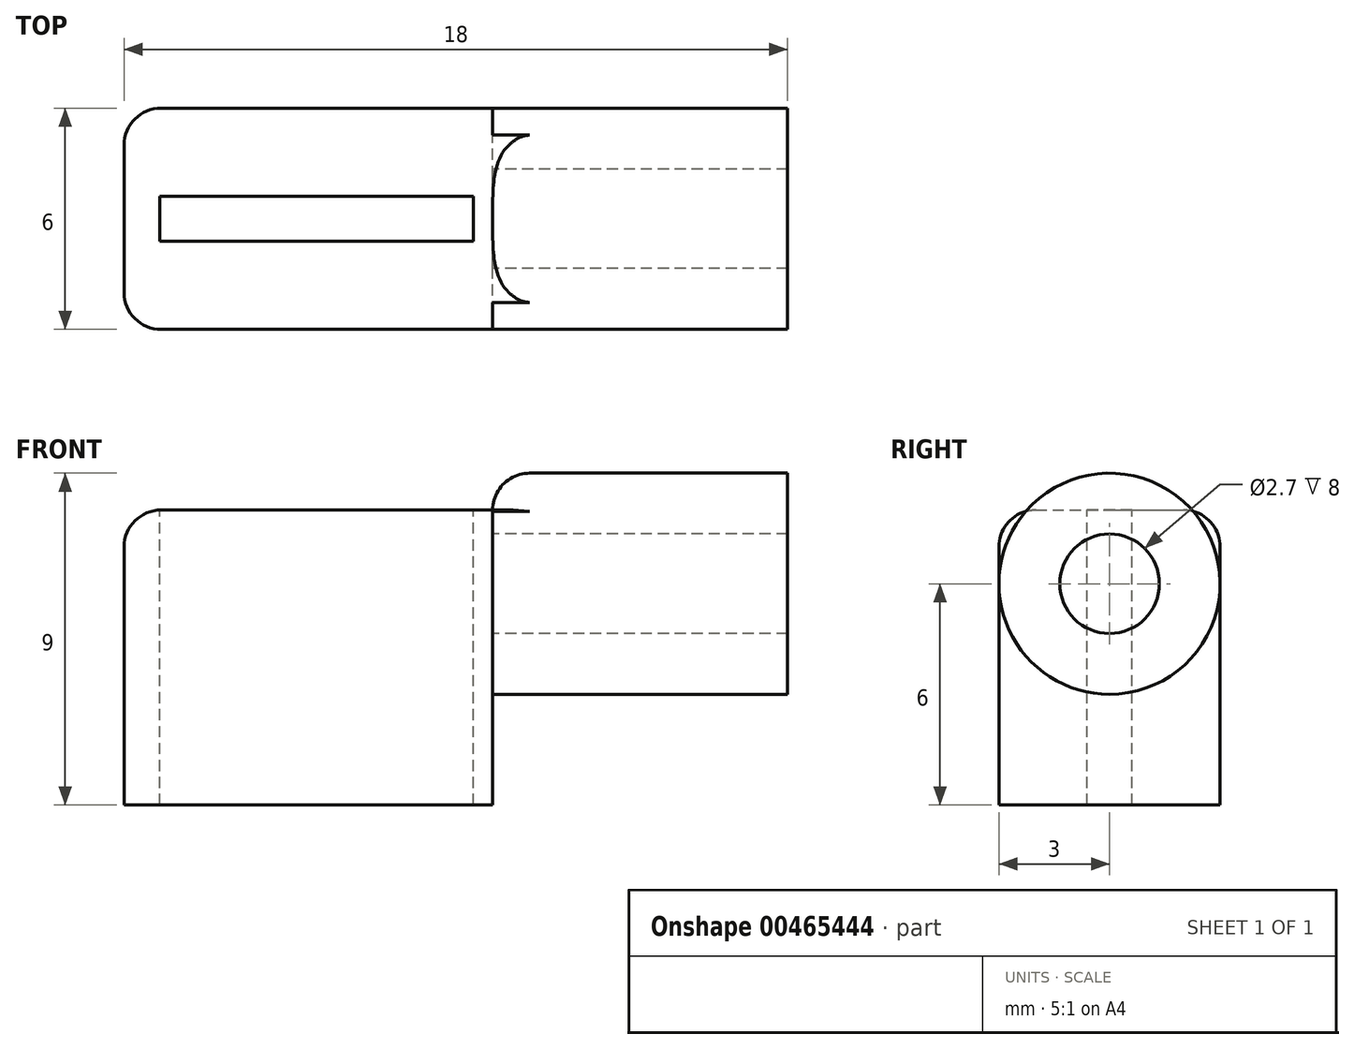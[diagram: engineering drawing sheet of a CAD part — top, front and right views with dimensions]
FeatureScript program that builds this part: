
annotation { "Feature Type Name" : "Feature", "Feature Type Description" : "" }
export const myFeature = defineFeature(function(context is Context, id is Id, definition is map)
    precondition{}
    {
        {
            var Q0;
            Q0=qCreatedBy(makeId("Right.planeOp"),FACE);
            var sketch = newSketch(context, id + "F0", { "sketchPlane" : qUnion([Q0])});
            skCircle(sketch, "E0", {"center": v(0, 0) * mm, "radius": 3 * mm});
            skCircle(sketch, "E1", {"center": v(0, 0) * mm, "radius": 1.35 * mm});
            skSolve(sketch);
        }
        {
            var Q0;
            Q0=makeQuery(id+"F0.imprint","IMPRINT",FACE,{"disambiguationData":[TD([[makeQuery(id+"F0.imprint","IMPRINT",EDGE,{"derivedFrom":sQuery(id+"F0.wireOp",EDGE,"E0")}),1.0]])]});
            extrude(context, id + "F1", {"entities" : qUnion([Q0]), "depth" : 8 * mm});
        }
        {
            var Q0;
            Q0=qCreatedBy(makeId("Top.planeOp"),FACE);
            var sketch = newSketch(context, id + "F2", { "sketchPlane" : qUnion([Q0])});
            skLineSegment(sketch, "E2.bottom", {"start": v(0, -3) * mm, "end": v(-10, -3) * mm});
            skLineSegment(sketch, "E2.top", {"start": v(0, 3) * mm, "end": v(-10, 3) * mm});
            skLineSegment(sketch, "E2.left", {"start": v(0, -3) * mm, "end": v(0, 3) * mm});
            skLineSegment(sketch, "E2.right", {"start": v(-10, -3) * mm, "end": v(-10, 3) * mm});
            skSolve(sketch);
        }
        {
            var Q0;
            Q0=makeQuery(id+"F2.imprint","IMPRINT",FACE,{"disambiguationData":[TD([[makeQuery(id+"F2.imprint","IMPRINT",EDGE,{"derivedFrom":sQuery(id+"F2.wireOp",EDGE,"E2.bottom")}),-1.0]])]});
            extrude(context, id + "F3", {"entities" : qUnion([Q0]), "operationType" : NewBodyOperationType.ADD, "depth" : 2 * mm});
        }
        {
            var Q0;
            Q0=makeQuery(id+"F3.opExtrude","CAP_FACE",FACE,{"disambiguationData":[OSD([sQuery(id+"F2.wireOp",EDGE,"E2.bottom"),sQuery(id+"F2.wireOp",EDGE,"E2.top"),sQuery(id+"F2.wireOp",EDGE,"E2.left"),sQuery(id+"F2.wireOp",EDGE,"E2.right")])],"isStart":true});
            extrude(context, id + "F4", {"entities" : qUnion([Q0]), "operationType" : NewBodyOperationType.ADD, "depth" : 6 * mm});
        }
        {
            var Q0;
            Q0=makeQuery(id+"F3.opExtrude","CAP_FACE",FACE,{"disambiguationData":[OSD([sQuery(id+"F2.wireOp",EDGE,"E2.bottom"),sQuery(id+"F2.wireOp",EDGE,"E2.top"),sQuery(id+"F2.wireOp",EDGE,"E2.left"),sQuery(id+"F2.wireOp",EDGE,"E2.right")])],"isStart":false});
            var sketch = newSketch(context, id + "F5", { "sketchPlane" : qUnion([Q0])});
            skLineSegment(sketch, "E3.bottom", {"start": v(-9.03, 0.61) * mm, "end": v(-0.53, 0.61) * mm});
            skLineSegment(sketch, "E3.top", {"start": v(-9.03, -0.61) * mm, "end": v(-0.53, -0.61) * mm});
            skLineSegment(sketch, "E3.left", {"start": v(-9.03, 0.61) * mm, "end": v(-9.03, -0.61) * mm});
            skLineSegment(sketch, "E3.right", {"start": v(-0.53, 0.61) * mm, "end": v(-0.53, -0.61) * mm});
            skSolve(sketch);
        }
        {
            var Q0;
            {var subQ10=sQuery(id+"F5.wireOp",EDGE,"E3.bottom");Q0=makeQuery(id+"F5.imprint","IMPRINT",FACE,{"disambiguationData":[TD([[makeQuery(id+"F5.imprint","IMPRINT",EDGE,{"derivedFrom":subQ10}),-1.0]])]});}
            extrude(context, id + "F6", {"entities" : qUnion([Q0]), "operationType" : NewBodyOperationType.REMOVE, "oppositeDirection" : true, "depth" : 8 * mm});
        }
        {
            var Q0;
            Q0=makeQuery(id+"F3.opExtrude","CAP_EDGE",EDGE,{"disambiguationData":[OSD([sQuery(id+"F2.wireOp",EDGE,"E2.right")])],"isStart":false});
            var Q1;
            Q1=makeQuery(id+"F3.opExtrude","CAP_EDGE",EDGE,{"disambiguationData":[OSD([sQuery(id+"F2.wireOp",EDGE,"E2.bottom")])],"isStart":false});
            var Q2;
            Q2=makeQuery(id+"F3.opExtrude","CAP_EDGE",EDGE,{"disambiguationData":[OSD([sQuery(id+"F2.wireOp",EDGE,"E2.top")])],"isStart":false});
            fillet(context, id + "F7", {"entities" : qUnion([Q0, Q1, Q2]), "radius" : 1 * mm, "tangentPropagation" : true, "allowEdgeOverflow" : false});
        }
        {
            var Q0;
            {var subQ0=sQuery(id+"F0.wireOp",EDGE,"E0");var subQ1=makeQuery(id+"F1.opExtrude","SWEPT_FACE",FACE,{"disambiguationData":[OSD([subQ0])]});var subQ2=sQuery(id+"F2.wireOp",EDGE,"E2.left");var subQ3=makeQuery(id+"F1.opExtrude","CAP_FACE",FACE,{"disambiguationData":[OSD([subQ0,sQuery(id+"F0.wireOp",EDGE,"E1")])],"isStart":true});Q0=makeQuery(id+"F3.boolean.opBoolean","SPLIT",EDGE,{"disambiguationData":[topologyDisambiguationEdgeConnected([subQ1,subQ3]),TD([makeQuery(id+"F3.opExtrude","CAP_FACE",FACE,{"disambiguationData":[OSD([sQuery(id+"F2.wireOp",EDGE,"E2.bottom"),sQuery(id+"F2.wireOp",EDGE,"E2.top"),subQ2,sQuery(id+"F2.wireOp",EDGE,"E2.right")])],"isStart":false})])],"derivedFrom":makeQuery(id+"F1.opExtrude","CAP_EDGE",EDGE,{"disambiguationData":[OSD([subQ0])],"isStart":true})});}
            fillet(context, id + "F8", {"entities" : qUnion([Q0]), "radius" : 1 * mm, "tangentPropagation" : true, "allowEdgeOverflow" : false});
        }
        {
            var Q0;
            {var subQ0=sQuery(id+"F2.wireOp",EDGE,"E2.right");var subQ1=sQuery(id+"F2.wireOp",EDGE,"E2.top");Q0=makeQuery(id+"F4.boolean.opBoolean","MERGE",EDGE,{"derivedFrom":[makeQuery(id+"F3.opExtrude","SWEPT_EDGE",EDGE,{"disambiguationData":[OSD([subQ1,subQ0])]}),makeQuery(id+"F4.opExtrude","SWEPT_EDGE",EDGE,{"disambiguationData":[OSD([subQ1,subQ0])]})]});}
            var Q1;
            {var subQ0=sQuery(id+"F2.wireOp",EDGE,"E2.right");var subQ1=sQuery(id+"F2.wireOp",EDGE,"E2.bottom");Q1=makeQuery(id+"F4.boolean.opBoolean","MERGE",EDGE,{"derivedFrom":[makeQuery(id+"F3.opExtrude","SWEPT_EDGE",EDGE,{"disambiguationData":[OSD([subQ1,subQ0])]}),makeQuery(id+"F4.opExtrude","SWEPT_EDGE",EDGE,{"disambiguationData":[OSD([subQ1,subQ0])]})]});}
            fillet(context, id + "F9", {"entities" : qUnion([Q0, Q1]), "radius" : 1 * mm, "tangentPropagation" : true, "allowEdgeOverflow" : false});
        }
    });
